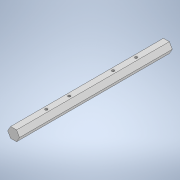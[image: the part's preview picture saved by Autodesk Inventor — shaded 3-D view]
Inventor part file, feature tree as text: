
AUTODESK INVENTOR PART (.ipt)
format: ipt  version: 2022 (Build 260153000, 153)  size: 125,440 bytes
history: native  units: mm
features: extrude x2, sketch x2
ambient origin geometry x8: Origin, YZ Plane, XZ Plane, XY Plane, X Axis, Y Axis, Z Axis, Center Point
bodies: Body1 (feature_tree)
feature tree (4):
  extrude  "Extrusion5"  Depth=3.1mm TaperAngle=360.0deg
  extrude  "Extrusion6"  Depth=80.0mm
  sketch  "Sketch4"  dims[d15=3.1mm d16=60.0mm d18=360.0deg]
  sketch  "Sketch5"  dims[d20=80.0mm d21=0.0mm d22=1.3mm d23=64.1mm d24=52.1mm d25=29.1mm d26=17.1mm d27=6.0mm d28=0.0mm]
